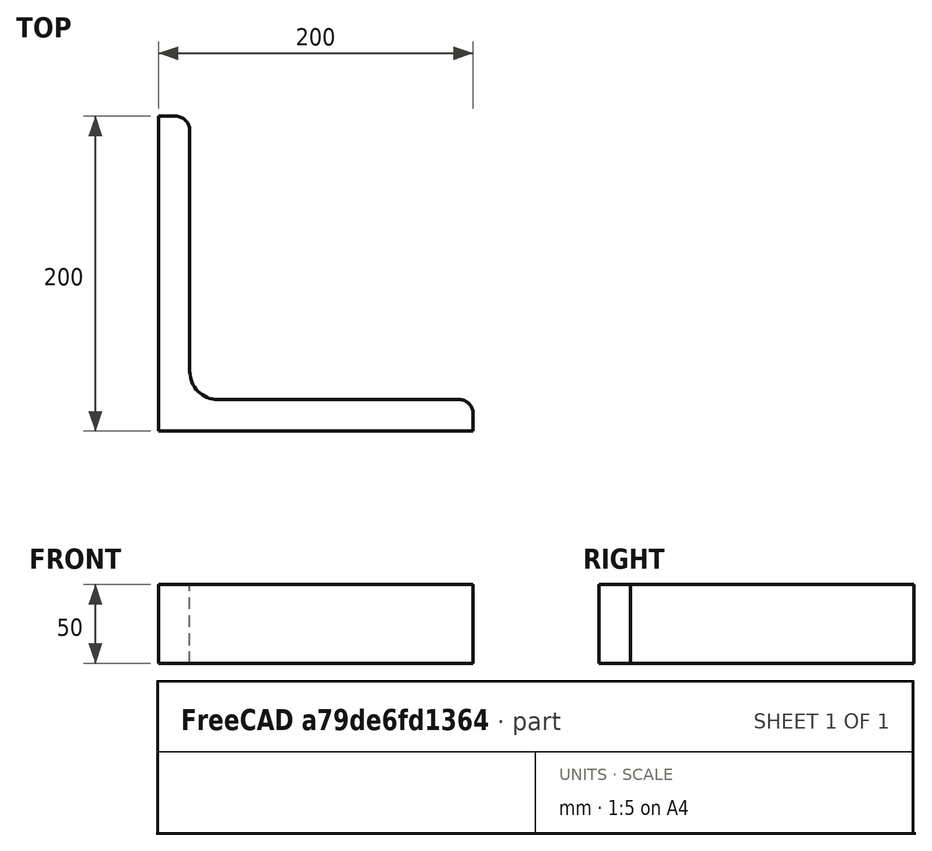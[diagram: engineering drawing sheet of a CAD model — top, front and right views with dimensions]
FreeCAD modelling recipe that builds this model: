
FCSTD DOCUMENT  (FreeCAD 0.15R4671 (Git))
Label: Angle Bar L200x200x20 EN10056 S235JR
License: All rights reserved
LicenseURL: http://en.wikipedia.org/wiki/All_rights_reserved
objects: Sketcher::SketchObject×1, Part::Extrusion×1
note: 2 computed .brp shape members not serialized (recipe doc carries the construction recipe); baked Part::Feature solids carry a one-line shape summary decoded from their .brp

FEATURE [Sketcher::SketchObject] Sketch
  sketch-geometry (9):
    g0: LineSegment StartX=0 StartY=0 StartZ=0 EndX=200 EndY=0 EndZ=0
    g1: LineSegment StartX=200 StartY=0 StartZ=0 EndX=200 EndY=11 EndZ=0
    g2: LineSegment StartX=191 StartY=20 StartZ=0 EndX=38 EndY=20 EndZ=0
    g3: LineSegment StartX=0 StartY=0 StartZ=0 EndX=0 EndY=200 EndZ=0
    g4: LineSegment StartX=0 StartY=200 StartZ=0 EndX=11 EndY=200 EndZ=0
    g5: LineSegment StartX=20 StartY=191 StartZ=0 EndX=20 EndY=38 EndZ=0
    g6: ArcOfCircle CenterX=38 CenterY=38 CenterZ=0 NormalX=0 NormalY=0 NormalZ=1 Radius=18 StartAngle=3.14159 EndAngle=4.71239
    g7: ArcOfCircle CenterX=11 CenterY=191 CenterZ=0 NormalX=0 NormalY=0 NormalZ=1 Radius=9 StartAngle=0 EndAngle=1.5708
    g8: ArcOfCircle CenterX=191 CenterY=11 CenterZ=0 NormalX=0 NormalY=0 NormalZ=1 Radius=9 StartAngle=0 EndAngle=1.5708
  constraints (23):
    c: Coincident(g0,g-1)
    c: Horizontal(g0)
    c: Coincident(g1,g0)
    c: Vertical(g1)
    c: Horizontal(g2)
    c: Coincident(g3,g-1)
    c: Vertical(g3)
    c: Coincident(g4,g3)
    c: Horizontal(g4)
    c: Vertical(g5)
    c: Tangent(g5,g6) = -1.5708
    c: Tangent(g2,g6) = 1.5708
    c: Tangent(g4,g7) = 1.5708
    c: Tangent(g5,g7) = 1.5708
    c: Tangent(g2,g8) = -1.5708
    c: Tangent(g1,g8) = -1.5708
    c: DistanceX(g0) = 200
    c: DistanceY(g3) = 200
    c: DistanceY(g0,g2) = 20
    c: DistanceX(g3,g5) = 20
    c: Radius(g6) = 18
    c: Radius(g8) = 9
    c: Radius(g7) = 9
FEATURE [Part::Extrusion] Extrude  label="Angle Bar L200x200x20 EN10056 S235JR"
  Base = -> Sketch
  Dir = (0,0,50)
  Solid = true
